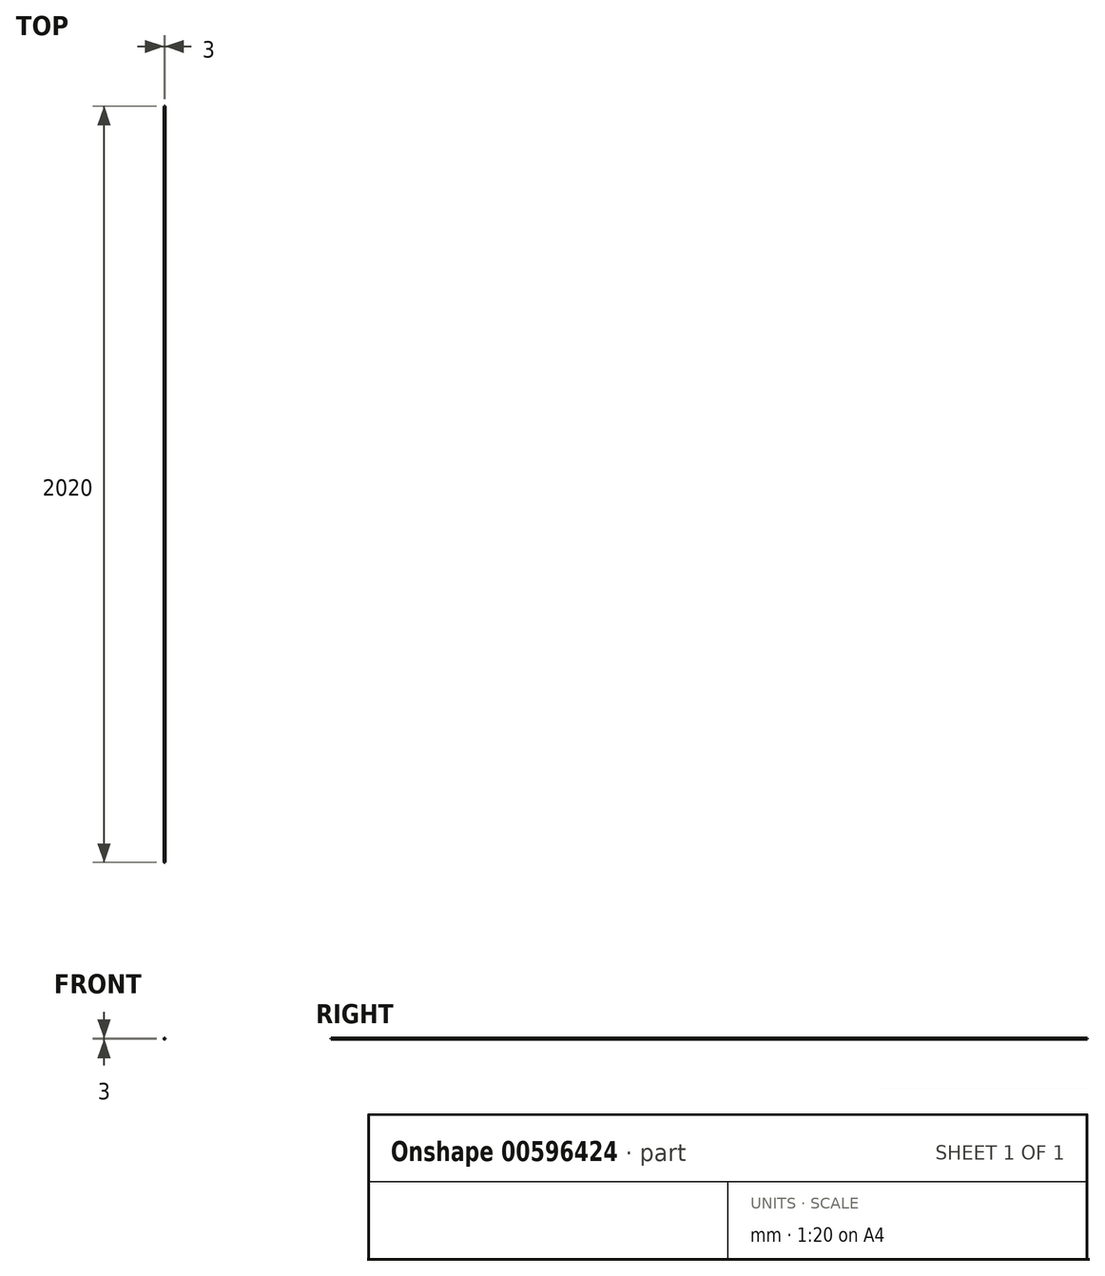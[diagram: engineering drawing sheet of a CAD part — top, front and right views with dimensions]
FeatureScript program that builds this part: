
annotation { "Feature Type Name" : "Feature", "Feature Type Description" : "" }
export const myFeature = defineFeature(function(context is Context, id is Id, definition is map)
    precondition{}
    {
        {
            var Q0;
            Q0=qCreatedBy(makeId("Front.planeOp"),FACE);
            var sketch = newSketch(context, id + "F0", { "sketchPlane" : qUnion([Q0])});
            skCircle(sketch, "E0", {"center": v(0, 0) * mm, "radius": 1.5 * mm});
            skSolve(sketch);
        }
        {
            var Q0;
            Q0=makeQuery(id+"F0.imprint","IMPRINT",FACE,{"disambiguationData":[TD([[makeQuery(id+"F0.imprint","IMPRINT",EDGE,{"derivedFrom":sQuery(id+"F0.wireOp",EDGE,"E0")}),1.0]])]});
            extrude(context, id + "F1", {"entities" : qUnion([Q0]), "depth" : 2020 * mm, "offsetDistance" : 25 * mm});
        }
    });
